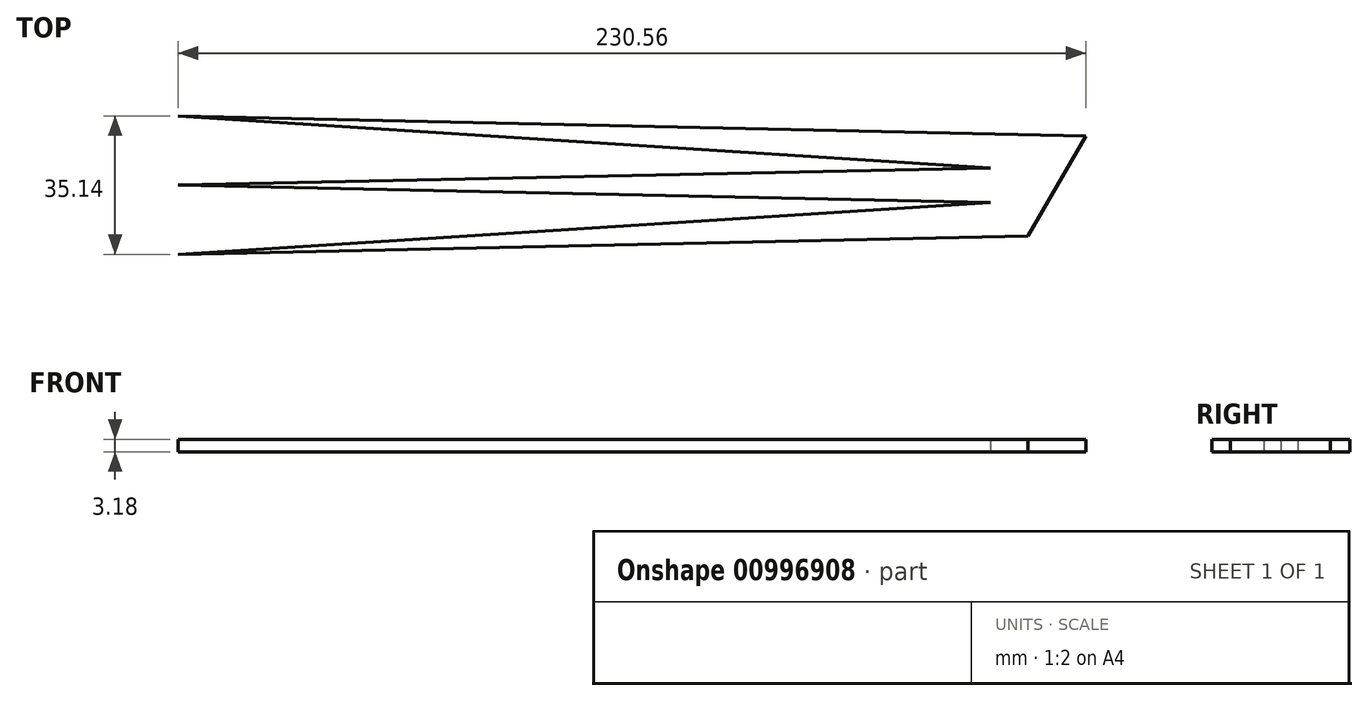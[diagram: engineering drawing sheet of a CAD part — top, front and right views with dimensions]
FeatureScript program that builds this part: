
annotation { "Feature Type Name" : "Feature", "Feature Type Description" : "" }
export const myFeature = defineFeature(function(context is Context, id is Id, definition is map)
    precondition{}
    {
        {
            var Q0;
            Q0=qCreatedBy(makeId("Top.planeOp"),FACE);
            var sketch = newSketch(context, id + "F0", { "sketchPlane" : qUnion([Q0])});
            skLineSegment(sketch, "E0", {"start": v(-7.42, -12.86) * mm, "end": v(-223.32, -17.57) * mm});
            skLineSegment(sketch, "E1", {"start": v(-223.32, -17.57) * mm, "end": v(-16.95, -4.36) * mm});
            skLineSegment(sketch, "E2", {"start": v(-16.95, -4.36) * mm, "end": v(-223.32, 0) * mm});
            skLineSegment(sketch, "E3", {"start": v(-223.32, 0) * mm, "end": v(-16.95, 4.36) * mm});
            skLineSegment(sketch, "E4", {"start": v(-16.95, 4.36) * mm, "end": v(-223.32, 17.57) * mm});
            skLineSegment(sketch, "E5", {"start": v(-223.32, 17.57) * mm, "end": v(7.24, 12.54) * mm});
            skLineSegment(sketch, "E6", {"start": v(-223.32, 0) * mm, "end": v(-223.32, -17.57) * mm, "construction": true});
            skLineSegment(sketch, "E7", {"start": v(-223.32, 17.57) * mm, "end": v(-223.32, 0) * mm, "construction": true});
            skLineSegment(sketch, "E8", {"start": v(-7.42, -12.86) * mm, "end": v(7.24, 12.54) * mm});
            skLineSegment(sketch, "E9", {"start": v(-7.42, -12.86) * mm, "end": v(114.14, -12.86) * mm, "construction": true});
            skLineSegment(sketch, "E10", {"start": v(-16.95, 4.36) * mm, "end": v(-16.4, 13.06) * mm, "construction": true});
            skLineSegment(sketch, "E11", {"start": v(-16.95, -4.36) * mm, "end": v(-16.4, -13.06) * mm, "construction": true});
            skLineSegment(sketch, "E12", {"start": v(-16.95, 4.36) * mm, "end": v(-16.95, -4.36) * mm, "construction": true});
            skSolve(sketch);
        }
        {
            var Q0;
            Q0 = qSketchRegion(id + "F0", true);
            extrude(context, id + "F1", {"entities" : qUnion([Q0]), "endBound" : BoundingType.SYMMETRIC, "depth" : 3.17 * mm, "offsetDistance" : 25.4 * mm});
        }
    });
